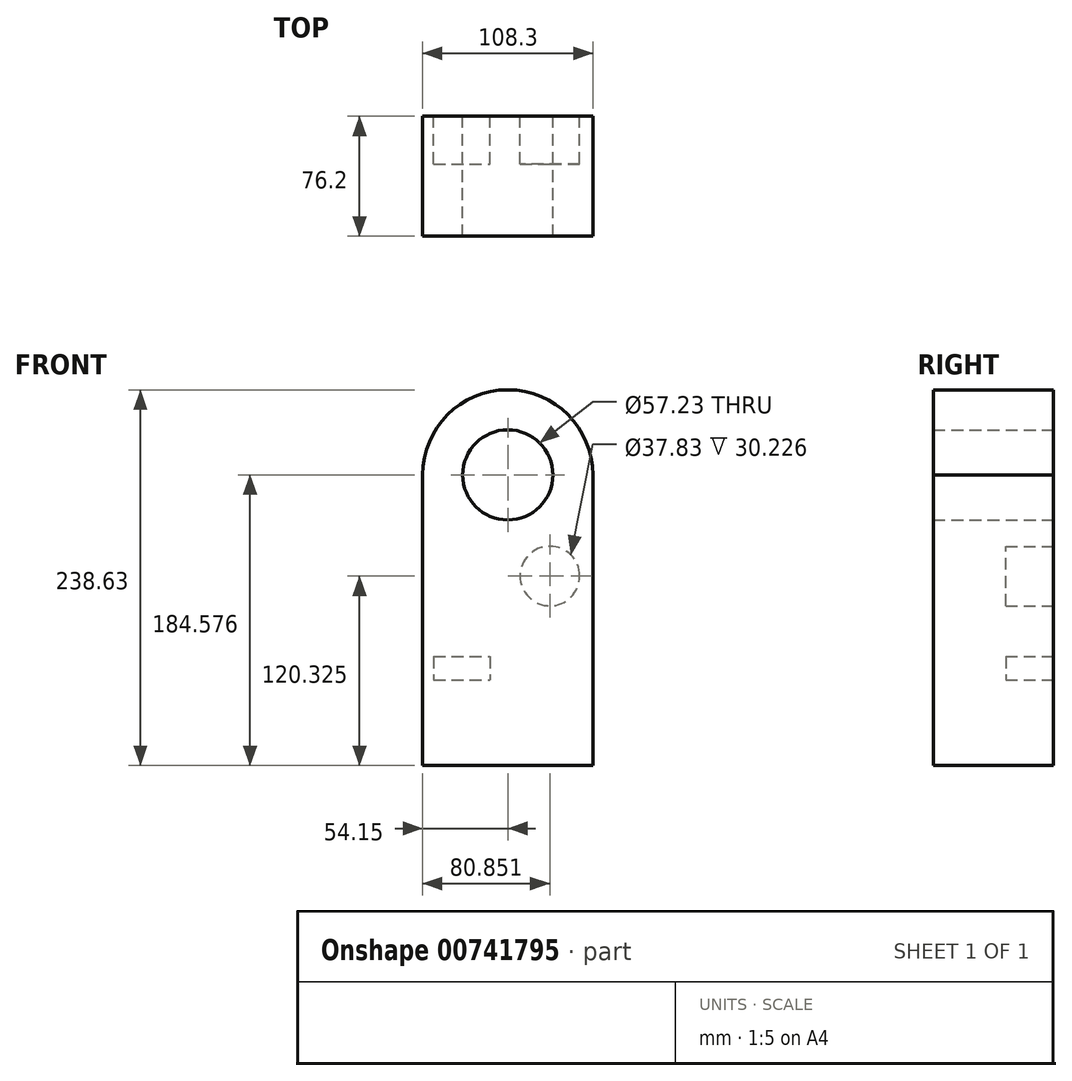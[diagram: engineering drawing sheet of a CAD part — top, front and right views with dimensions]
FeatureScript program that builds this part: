
annotation { "Feature Type Name" : "Feature", "Feature Type Description" : "" }
export const myFeature = defineFeature(function(context is Context, id is Id, definition is map)
    precondition{}
    {
        {
            var Q0;
            Q0=qCreatedBy(makeId("Front.planeOp"),FACE);
            var sketch = newSketch(context, id + "F0", { "sketchPlane" : qUnion([Q0])});
            skLineSegment(sketch, "E0.bottom", {"start": v(-54.15, 92.29) * mm, "end": v(-54.05, 92.29) * mm});
            skLineSegment(sketch, "E0.top", {"start": v(-54.15, -92.29) * mm, "end": v(54.15, -92.29) * mm});
            skLineSegment(sketch, "E0.left", {"start": v(-54.15, 92.29) * mm, "end": v(-54.15, -92.29) * mm});
            skLineSegment(sketch, "E0.right", {"start": v(54.15, 92.29) * mm, "end": v(54.15, -92.29) * mm});
            skPoint(sketch, "E0.middle", {"position": v(0, 0) * mm});
            skArc(sketch, "E1", {"start": v(54.05, 92.29) * mm, "mid": v(0, 146.34) * mm, "end": v(-54.05, 92.29) * mm});
            skCircle(sketch, "E2", {"center": v(0, 92.29) * mm, "radius": 28.61 * mm});
            skLineSegment(sketch, "E3.trimOffspring", {"start": v(54.05, 92.29) * mm, "end": v(54.15, 92.29) * mm});
            skSolve(sketch);
        }
        {
            var Q0;
            Q0 = qSketchRegion(id + "F0", true);
            extrude(context, id + "F1", {"entities" : qUnion([Q0]), "depth" : 76.2 * mm, "offsetDistance" : 25.4 * mm});
        }
        {
            var Q0;
            Q0=qCreatedBy(makeId("Front.planeOp"),FACE);
            var sketch = newSketch(context, id + "F2", { "sketchPlane" : qUnion([Q0])});
            skCircle(sketch, "E4", {"center": v(26.7, 28.03) * mm, "radius": 18.91 * mm});
            skSolve(sketch);
        }
        {
            var Q0;
            Q0=qCreatedBy(makeId("Front.planeOp"),FACE);
            var sketch = newSketch(context, id + "F3", { "sketchPlane" : qUnion([Q0])});
            skLineSegment(sketch, "E5.bottom", {"start": v(-47.2, -23.06) * mm, "end": v(-11.4, -23.06) * mm});
            skLineSegment(sketch, "E5.top", {"start": v(-47.2, -38.07) * mm, "end": v(-11.4, -38.07) * mm});
            skLineSegment(sketch, "E5.left", {"start": v(-47.2, -23.06) * mm, "end": v(-47.2, -38.07) * mm});
            skLineSegment(sketch, "E5.right", {"start": v(-11.4, -23.06) * mm, "end": v(-11.4, -38.07) * mm});
            skPoint(sketch, "E5.middle", {"position": v(-29.3, -30.56) * mm});
            skSolve(sketch);
        }
        {
            var Q0;
            Q0 = qSketchRegion(id + "F3", true);
            var Q1;
            Q1=makeQuery(id+"F2.imprint","IMPRINT",FACE,{"disambiguationData":[TD([[makeQuery(id+"F2.imprint","IMPRINT",EDGE,{"derivedFrom":sQuery(id+"F2.wireOp",EDGE,"E4")}),1.0]])]});
            extrude(context, id + "F4", {"entities" : qUnion([Q0, Q1]), "operationType" : NewBodyOperationType.REMOVE, "depth" : 30.23 * mm, "offsetDistance" : 25.4 * mm});
        }
    });
